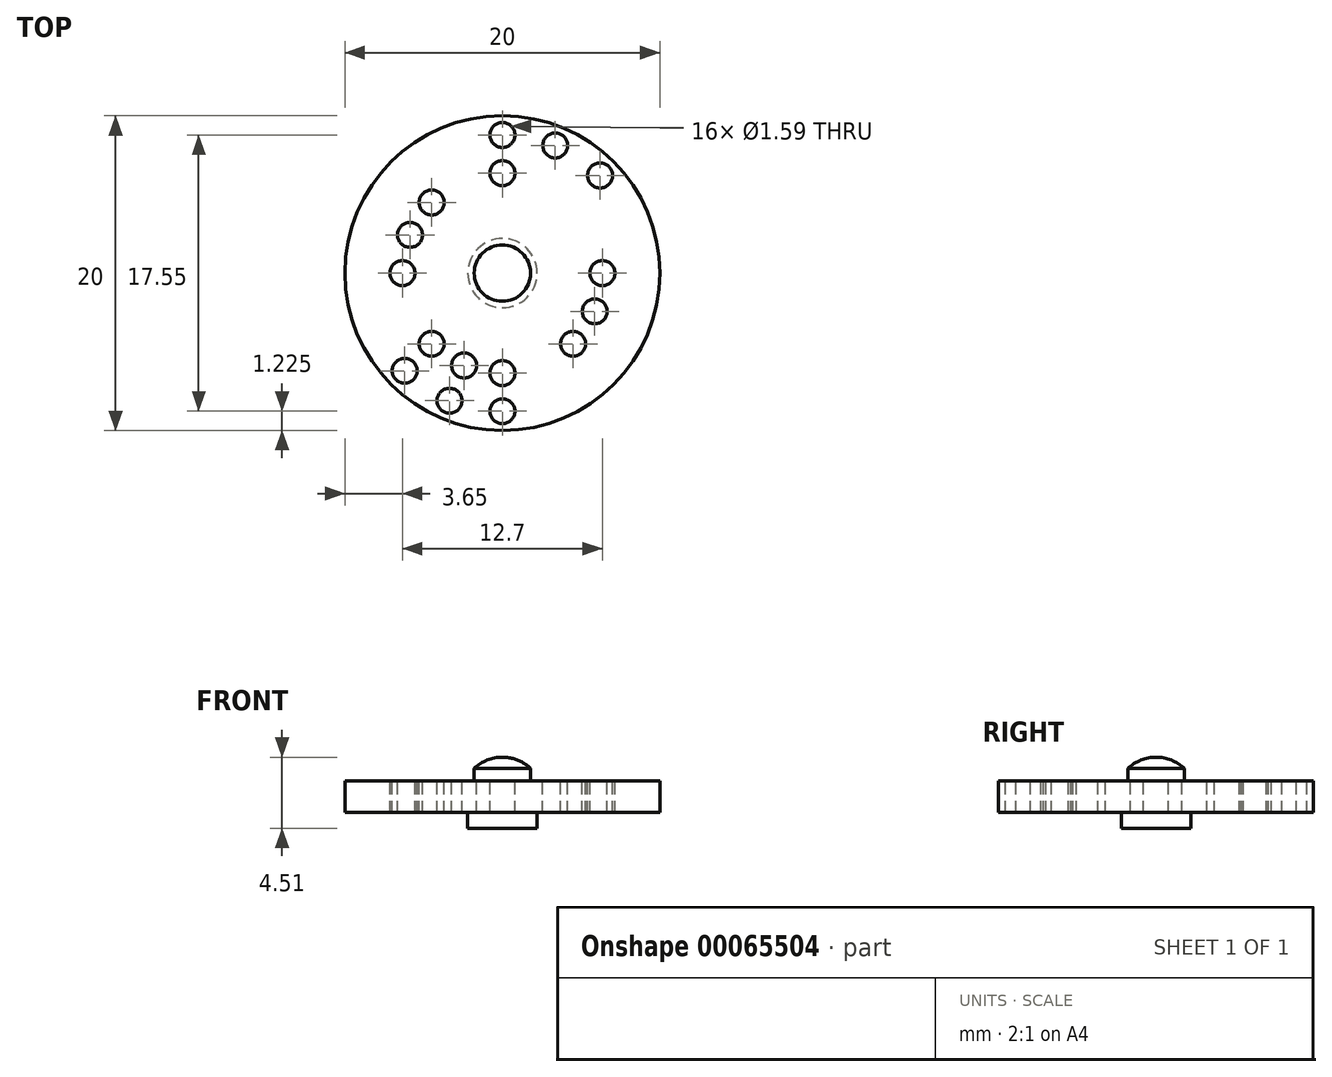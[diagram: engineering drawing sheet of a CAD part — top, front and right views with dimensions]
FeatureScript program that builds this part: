
annotation { "Feature Type Name" : "Feature", "Feature Type Description" : "" }
export const myFeature = defineFeature(function(context is Context, id is Id, definition is map)
    precondition{}
    {
        {
            var Q0;
            Q0=qCreatedBy(makeId("Front.planeOp"),FACE);
            var sketch = newSketch(context, id + "F0", { "sketchPlane" : qUnion([Q0])});
            skLineSegment(sketch, "E0", {"start": v(0, 0) * mm, "end": v(10, 0) * mm});
            skLineSegment(sketch, "E1", {"start": v(10, 0) * mm, "end": v(10, -2) * mm});
            skLineSegment(sketch, "E2", {"start": v(10, -2) * mm, "end": v(2.2, -2) * mm});
            skLineSegment(sketch, "E3", {"start": v(2.2, -2) * mm, "end": v(2.2, -3) * mm});
            skLineSegment(sketch, "E4", {"start": v(2.2, -3) * mm, "end": v(0, -3) * mm});
            skLineSegment(sketch, "E5", {"start": v(0, -3) * mm, "end": v(0, 0) * mm});
            skLineSegment(sketch, "E6", {"start": v(1.79, 0) * mm, "end": v(1.79, 0.8) * mm});
            skLineSegment(sketch, "E7", {"start": v(1.79, 0.8) * mm, "end": v(0, 0.8) * mm});
            skLineSegment(sketch, "E8", {"start": v(0, 0.8) * mm, "end": v(0, 0) * mm});
            skSolve(sketch);
        }
        {
            var Q0;
            {var subQ2=sQuery(id+"F0.wireOp",EDGE,"E6");Q0=makeQuery(id+"F0.imprint","IMPRINT",FACE,{"disambiguationData":[TD([[makeQuery(id+"F0.imprint","IMPRINT",EDGE,{"derivedFrom":subQ2}),1.0]])]});}
            var Q1;
            {var subQ0=sQuery(id+"F0.wireOp",EDGE,"E1");Q1=makeQuery(id+"F0.imprint","IMPRINT",FACE,{"disambiguationData":[TD([[makeQuery(id+"F0.imprint","IMPRINT",EDGE,{"derivedFrom":subQ0}),-1.0]])]});}
            var Q2;
            Q2=sQuery(id+"F0.wireOp",EDGE,"E5");
            revolve(context, id + "F1", {"entities" : qUnion([Q0, Q1]), "axis" : qUnion([Q2]), "revolveType" : RevolveType.FULL});
        }
        {
            var Q0;
            Q0=makeQuery(id+"F1.opRevolve","SWEPT_FACE",FACE,{"disambiguationData":[OSD([sQuery(id+"F0.wireOp",EDGE,"E0")])]});
            var sketch = newSketch(context, id + "F2", { "sketchPlane" : qUnion([Q0])});
            skLineSegment(sketch, "E9", {"start": v(0, 0) * mm, "end": v(0, 6.35) * mm});
            skCircle(sketch, "E10", {"center": v(0, 6.35) * mm, "radius": 0.8 * mm});
            skCircle(sketch, "E11.1.0", {"center": v(2.43, 5.87) * mm, "radius": 0.8 * mm});
            skCircle(sketch, "E11.2.0", {"center": v(4.5, 4.5) * mm, "radius": 0.8 * mm});
            skPoint(sketch, "E11.center", {"position": v(0, 0) * mm});
            skLineSegment(sketch, "E11.anchor1", {"start": v(0, 0) * mm, "end": v(0, 6.35) * mm, "construction": true});
            skLineSegment(sketch, "E11.anchor2", {"start": v(0, 0) * mm, "end": v(4.5, 4.5) * mm, "construction": true});
            skCircle(sketch, "E12.1.0", {"center": v(-6.35, 0) * mm, "radius": 0.8 * mm});
            skCircle(sketch, "E12.1.1", {"center": v(-5.87, 2.43) * mm, "radius": 0.8 * mm});
            skCircle(sketch, "E12.1.2", {"center": v(-4.5, 4.5) * mm, "radius": 0.8 * mm});
            skCircle(sketch, "E12.2.0", {"center": v(0, -6.35) * mm, "radius": 0.8 * mm});
            skCircle(sketch, "E12.2.1", {"center": v(-2.43, -5.87) * mm, "radius": 0.8 * mm});
            skCircle(sketch, "E12.2.2", {"center": v(-4.5, -4.5) * mm, "radius": 0.8 * mm});
            skCircle(sketch, "E12.3.0", {"center": v(6.35, 0) * mm, "radius": 0.8 * mm});
            skCircle(sketch, "E12.3.1", {"center": v(5.87, -2.43) * mm, "radius": 0.8 * mm});
            skCircle(sketch, "E12.3.2", {"center": v(4.5, -4.5) * mm, "radius": 0.8 * mm});
            skCircle(sketch, "E13", {"center": v(0, 8.78) * mm, "radius": 0.8 * mm});
            skLineSegment(sketch, "E14", {"start": v(0, 0) * mm, "end": v(2.43, 5.87) * mm});
            skLineSegment(sketch, "E15", {"start": v(0, 0) * mm, "end": v(3.83, 9.24) * mm});
            skLineSegment(sketch, "E16", {"start": v(0, 0) * mm, "end": v(4.5, 4.5) * mm});
            skLineSegment(sketch, "E17", {"start": v(0, 0) * mm, "end": v(7.07, 7.07) * mm});
            skCircle(sketch, "E18.1.0", {"center": v(3.36, 8.1) * mm, "radius": 0.8 * mm});
            skCircle(sketch, "E18.2.0", {"center": v(6.2, 6.2) * mm, "radius": 0.8 * mm});
            skLineSegment(sketch, "E18.anchor1", {"start": v(0, 0) * mm, "end": v(0, 8.78) * mm, "construction": true});
            skLineSegment(sketch, "E18.anchor2", {"start": v(0, 0) * mm, "end": v(6.2, 6.2) * mm, "construction": true});
            skCircle(sketch, "E19.1.0", {"center": v(0, -8.78) * mm, "radius": 0.8 * mm});
            skCircle(sketch, "E19.1.1", {"center": v(-3.36, -8.1) * mm, "radius": 0.8 * mm});
            skCircle(sketch, "E19.1.2", {"center": v(-6.2, -6.2) * mm, "radius": 0.8 * mm});
            skSolve(sketch);
        }
        {
            var Q0;
            Q0=makeQuery(id+"F2.imprint","IMPRINT",FACE,{"disambiguationData":[TD([[makeQuery(id+"F2.imprint","IMPRINT",EDGE,{"derivedFrom":sQuery(id+"F2.wireOp",EDGE,"E12.1.0")}),1.0]])]});
            var Q1;
            Q1=makeQuery(id+"F2.imprint","IMPRINT",FACE,{"disambiguationData":[TD([[makeQuery(id+"F2.imprint","IMPRINT",EDGE,{"derivedFrom":sQuery(id+"F2.wireOp",EDGE,"E12.1.1")}),1.0]])]});
            var Q2;
            Q2=makeQuery(id+"F2.imprint","IMPRINT",FACE,{"disambiguationData":[TD([[makeQuery(id+"F2.imprint","IMPRINT",EDGE,{"derivedFrom":sQuery(id+"F2.wireOp",EDGE,"E12.1.2")}),1.0]])]});
            var Q3;
            Q3=makeQuery(id+"F2.imprint","IMPRINT",FACE,{"disambiguationData":[TD([[makeQuery(id+"F2.imprint","IMPRINT",EDGE,{"derivedFrom":sQuery(id+"F2.wireOp",EDGE,"E13")}),1.0]])]});
            var Q4;
            Q4=makeQuery(id+"F2.imprint","IMPRINT",FACE,{"disambiguationData":[TD([[makeQuery(id+"F2.imprint","IMPRINT",EDGE,{"derivedFrom":sQuery(id+"F2.wireOp",EDGE,"E10")}),1.0]])]});
            var Q5;
            {var subQ0=sQuery(id+"F2.wireOp",EDGE,"E15");var subQ4=makeQuery(id+"F2.imprint","IMPRINT",VERTEX,{"derivedFrom":subQ0});Q5=makeQuery(id+"F2.imprint","IMPRINT",FACE,{"disambiguationData":[TD([[makeQuery(id+"F2.imprint","IMPRINT",EDGE,{"disambiguationData":[TD([[subQ4,1.0]])],"derivedFrom":subQ0}),-1.0]])]});}
            var Q6;
            {var subQ0=sQuery(id+"F2.wireOp",EDGE,"E15");var subQ4=makeQuery(id+"F2.imprint","IMPRINT",VERTEX,{"derivedFrom":subQ0});Q6=makeQuery(id+"F2.imprint","IMPRINT",FACE,{"disambiguationData":[TD([[makeQuery(id+"F2.imprint","IMPRINT",EDGE,{"disambiguationData":[TD([[subQ4,1.0]])],"derivedFrom":subQ0}),1.0]])]});}
            var Q7;
            {var subQ0=sQuery(id+"F2.wireOp",EDGE,"E18.1.0");var subQ1=sQuery(id+"F2.wireOp",EDGE,"E15");var subQ2=makeQuery(id+"F2.imprint","INTERSECT",VERTEX,{"disambiguationData":[OD(0.0)],"derivedFrom":[subQ1,subQ0]});Q7=makeQuery(id+"F2.imprint","IMPRINT",FACE,{"disambiguationData":[TD([[makeQuery(id+"F2.imprint","IMPRINT",EDGE,{"disambiguationData":[TD([[subQ2,-1.0]])],"derivedFrom":subQ1}),1.0]])]});}
            var Q8;
            {var subQ0=sQuery(id+"F2.wireOp",EDGE,"E18.1.0");var subQ1=sQuery(id+"F2.wireOp",EDGE,"E15");var subQ2=makeQuery(id+"F2.imprint","INTERSECT",VERTEX,{"disambiguationData":[OD(0.0)],"derivedFrom":[subQ1,subQ0]});Q8=makeQuery(id+"F2.imprint","IMPRINT",FACE,{"disambiguationData":[TD([[makeQuery(id+"F2.imprint","IMPRINT",EDGE,{"disambiguationData":[TD([[subQ2,-1.0]])],"derivedFrom":subQ1}),-1.0]])]});}
            var Q9;
            {var subQ0=sQuery(id+"F2.wireOp",EDGE,"E18.2.0");var subQ1=sQuery(id+"F2.wireOp",EDGE,"E17");var subQ2=makeQuery(id+"F2.imprint","INTERSECT",VERTEX,{"disambiguationData":[OD(0.0)],"derivedFrom":[subQ1,subQ0]});Q9=makeQuery(id+"F2.imprint","IMPRINT",FACE,{"disambiguationData":[TD([[makeQuery(id+"F2.imprint","IMPRINT",EDGE,{"disambiguationData":[TD([[subQ2,-1.0]])],"derivedFrom":subQ1}),1.0]])]});}
            var Q10;
            {var subQ0=sQuery(id+"F2.wireOp",EDGE,"E18.2.0");var subQ1=sQuery(id+"F2.wireOp",EDGE,"E17");var subQ2=makeQuery(id+"F2.imprint","INTERSECT",VERTEX,{"disambiguationData":[OD(0.0)],"derivedFrom":[subQ1,subQ0]});Q10=makeQuery(id+"F2.imprint","IMPRINT",FACE,{"disambiguationData":[TD([[makeQuery(id+"F2.imprint","IMPRINT",EDGE,{"disambiguationData":[TD([[subQ2,-1.0]])],"derivedFrom":subQ1}),-1.0]])]});}
            var Q11;
            {var subQ0=sQuery(id+"F2.wireOp",EDGE,"E17");var subQ4=makeQuery(id+"F2.imprint","IMPRINT",VERTEX,{"derivedFrom":subQ0});Q11=makeQuery(id+"F2.imprint","IMPRINT",FACE,{"disambiguationData":[TD([[makeQuery(id+"F2.imprint","IMPRINT",EDGE,{"disambiguationData":[TD([[subQ4,1.0]])],"derivedFrom":subQ0}),1.0]])]});}
            var Q12;
            {var subQ0=sQuery(id+"F2.wireOp",EDGE,"E17");var subQ4=makeQuery(id+"F2.imprint","IMPRINT",VERTEX,{"derivedFrom":subQ0});Q12=makeQuery(id+"F2.imprint","IMPRINT",FACE,{"disambiguationData":[TD([[makeQuery(id+"F2.imprint","IMPRINT",EDGE,{"disambiguationData":[TD([[subQ4,1.0]])],"derivedFrom":subQ0}),-1.0]])]});}
            var Q13;
            Q13=makeQuery(id+"F2.imprint","IMPRINT",FACE,{"disambiguationData":[TD([[makeQuery(id+"F2.imprint","IMPRINT",EDGE,{"derivedFrom":sQuery(id+"F2.wireOp",EDGE,"E12.2.2")}),1.0]])]});
            var Q14;
            Q14=makeQuery(id+"F2.imprint","IMPRINT",FACE,{"disambiguationData":[TD([[makeQuery(id+"F2.imprint","IMPRINT",EDGE,{"derivedFrom":sQuery(id+"F2.wireOp",EDGE,"E12.2.1")}),1.0]])]});
            var Q15;
            Q15=makeQuery(id+"F2.imprint","IMPRINT",FACE,{"disambiguationData":[TD([[makeQuery(id+"F2.imprint","IMPRINT",EDGE,{"derivedFrom":sQuery(id+"F2.wireOp",EDGE,"E12.2.0")}),1.0]])]});
            var Q16;
            Q16=makeQuery(id+"F2.imprint","IMPRINT",FACE,{"disambiguationData":[TD([[makeQuery(id+"F2.imprint","IMPRINT",EDGE,{"derivedFrom":sQuery(id+"F2.wireOp",EDGE,"E19.1.0")}),1.0]])]});
            var Q17;
            Q17=makeQuery(id+"F2.imprint","IMPRINT",FACE,{"disambiguationData":[TD([[makeQuery(id+"F2.imprint","IMPRINT",EDGE,{"derivedFrom":sQuery(id+"F2.wireOp",EDGE,"E19.1.1")}),1.0]])]});
            var Q18;
            Q18=makeQuery(id+"F2.imprint","IMPRINT",FACE,{"disambiguationData":[TD([[makeQuery(id+"F2.imprint","IMPRINT",EDGE,{"derivedFrom":sQuery(id+"F2.wireOp",EDGE,"E19.1.2")}),1.0]])]});
            var Q19;
            Q19=makeQuery(id+"F2.imprint","IMPRINT",FACE,{"disambiguationData":[TD([[makeQuery(id+"F2.imprint","IMPRINT",EDGE,{"derivedFrom":sQuery(id+"F2.wireOp",EDGE,"E12.3.2")}),1.0]])]});
            var Q20;
            Q20=makeQuery(id+"F2.imprint","IMPRINT",FACE,{"disambiguationData":[TD([[makeQuery(id+"F2.imprint","IMPRINT",EDGE,{"derivedFrom":sQuery(id+"F2.wireOp",EDGE,"E12.3.1")}),1.0]])]});
            var Q21;
            Q21=makeQuery(id+"F2.imprint","IMPRINT",FACE,{"disambiguationData":[TD([[makeQuery(id+"F2.imprint","IMPRINT",EDGE,{"derivedFrom":sQuery(id+"F2.wireOp",EDGE,"E12.3.0")}),1.0]])]});
            extrude(context, id + "F3", {"entities" : qUnion([Q0, Q1, Q2, Q3, Q4, Q5, Q6, Q7, Q8, Q9, Q10, Q11, Q12, Q13, Q14, Q15, Q16, Q17, Q18, Q19, Q20, Q21]), "operationType" : NewBodyOperationType.REMOVE, "oppositeDirection" : true, "depth" : 25.4 * mm});
        }
        {
            var Q0;
            Q0=qCreatedBy(makeId("Front.planeOp"),FACE);
            var sketch = newSketch(context, id + "F4", { "sketchPlane" : qUnion([Q0])});
            skLineSegment(sketch, "E20.0", {"start": v(1.79, 0.8) * mm, "end": v(-1.79, 0.8) * mm});
            skArc(sketch, "E21", {"start": v(1.79, 0.8) * mm, "mid": v(0, 1.5) * mm, "end": v(-1.79, 0.8) * mm});
            skLineSegment(sketch, "E22", {"start": v(0, 0.8) * mm, "end": v(0, 1.5) * mm});
            skSolve(sketch);
        }
        {
            var Q0;
            {var subQ3=sQuery(id+"F4.wireOp",EDGE,"E22");Q0=makeQuery(id+"F4.imprint","IMPRINT",FACE,{"disambiguationData":[TD([[makeQuery(id+"F4.imprint","IMPRINT",EDGE,{"derivedFrom":subQ3}),1.0]])]});}
            var Q1;
            Q1=sQuery(id+"F4.wireOp",EDGE,"E22");
            revolve(context, id + "F5", {"operationType" : NewBodyOperationType.ADD, "entities" : qUnion([Q0]), "axis" : qUnion([Q1]), "revolveType" : RevolveType.FULL});
        }
    });
